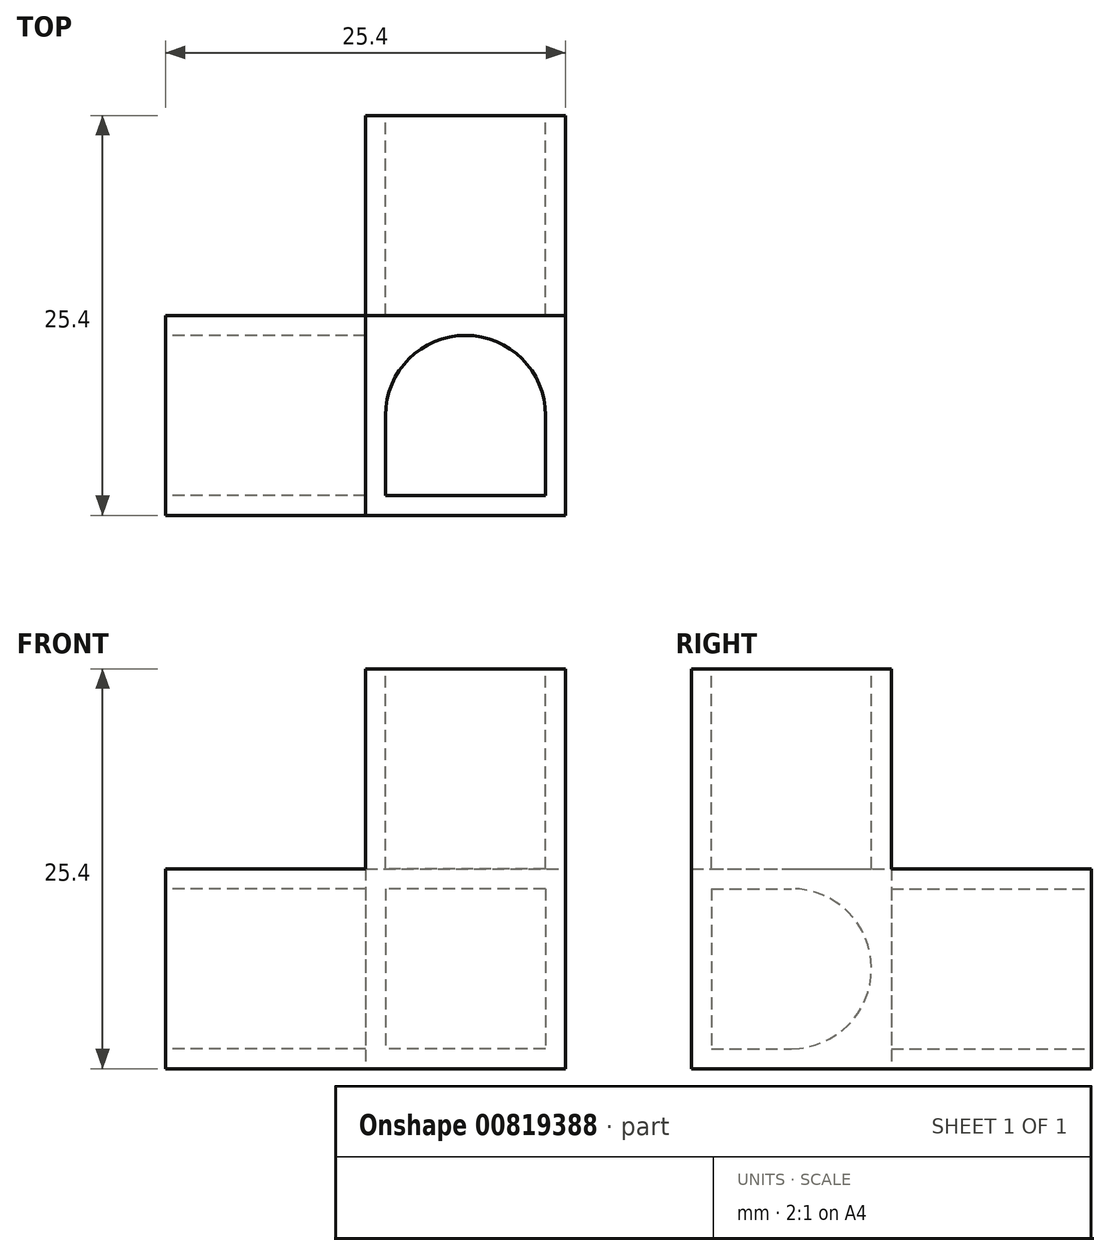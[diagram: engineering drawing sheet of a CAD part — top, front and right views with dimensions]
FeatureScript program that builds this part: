
annotation { "Feature Type Name" : "Feature", "Feature Type Description" : "" }
export const myFeature = defineFeature(function(context is Context, id is Id, definition is map)
    precondition{}
    {
        {
            var Q0;
            Q0=qCreatedBy(makeId("Top.planeOp"),FACE);
            var sketch = newSketch(context, id + "F0", { "sketchPlane" : qUnion([Q0])});
            skLineSegment(sketch, "E0", {"start": v(0, 0) * mm, "end": v(0, 12.7) * mm});
            skLineSegment(sketch, "E1", {"start": v(0, 12.7) * mm, "end": v(12.7, 12.7) * mm});
            skLineSegment(sketch, "E2", {"start": v(12.7, 12.7) * mm, "end": v(12.7, 25.4) * mm});
            skLineSegment(sketch, "E3", {"start": v(12.7, 25.4) * mm, "end": v(25.4, 25.4) * mm});
            skLineSegment(sketch, "E4", {"start": v(25.4, 25.4) * mm, "end": v(25.4, 12.7) * mm});
            skLineSegment(sketch, "E5", {"start": v(25.4, 0) * mm, "end": v(0, 0) * mm});
            skLineSegment(sketch, "E6", {"start": v(25.4, 0) * mm, "end": v(25.4, 12.7) * mm});
            skSolve(sketch);
        }
        {
            var Q0;
            Q0=qSketchRegion(id+"F0",true);
            extrude(context, id + "F1", {"entities" : qUnion([Q0]), "depth" : 12.7 * mm, "offsetDistance" : 25.4 * mm});
        }
        {
            var Q0;
            Q0=makeQuery(id+"F1.opExtrude","CAP_FACE",FACE,{"disambiguationData":[OSD([sQuery(id+"F0.wireOp",EDGE,"E0"),sQuery(id+"F0.wireOp",EDGE,"E1"),sQuery(id+"F0.wireOp",EDGE,"E2"),sQuery(id+"F0.wireOp",EDGE,"E3"),sQuery(id+"F0.wireOp",EDGE,"E4"),sQuery(id+"F0.wireOp",EDGE,"7KOMFThw-mYcV-5t9V-noh5-IcYA5axM13lC"),sQuery(id+"F0.wireOp",EDGE,"wvZKuQWc-6P0O-He2z-FqQs-M1QsOUskNR7B"),sQuery(id+"F0.wireOp",EDGE,"E5")])],"isStart":false});
            var sketch = newSketch(context, id + "F2", { "sketchPlane" : qUnion([Q0])});
            skLineSegment(sketch, "E7.bottom", {"start": v(12.7, 12.7) * mm, "end": v(25.4, 12.7) * mm});
            skLineSegment(sketch, "E7.top", {"start": v(12.7, 0) * mm, "end": v(25.4, 0) * mm});
            skLineSegment(sketch, "E7.left", {"start": v(12.7, 12.7) * mm, "end": v(12.7, 0) * mm});
            skLineSegment(sketch, "E7.right", {"start": v(25.4, 12.7) * mm, "end": v(25.4, 0) * mm});
            skSolve(sketch);
        }
        {
            var Q0;
            Q0=qSketchRegion(id+"F2",true);
            extrude(context, id + "F3", {"entities" : qUnion([Q0]), "operationType" : NewBodyOperationType.ADD, "depth" : 12.7 * mm, "offsetDistance" : 25.4 * mm});
        }
        {
            var Q0;
            Q0=makeQuery(id+"F1.opExtrude","SWEPT_FACE",FACE,{"disambiguationData":[OSD([sQuery(id+"F0.wireOp",EDGE,"E0")])]});
            var sketch = newSketch(context, id + "F4", { "sketchPlane" : qUnion([Q0])});
            skSolve(sketch);
        }
        {
            var Q0;
            Q0=makeQuery(id+"F3.opExtrude","CAP_FACE",FACE,{"disambiguationData":[OSD([sQuery(id+"F2.wireOp",EDGE,"E7.bottom"),sQuery(id+"F2.wireOp",EDGE,"E7.top"),sQuery(id+"F2.wireOp",EDGE,"E7.left"),sQuery(id+"F2.wireOp",EDGE,"E7.right")])],"isStart":false});
            var sketch = newSketch(context, id + "F5", { "sketchPlane" : qUnion([Q0])});
            skLineSegment(sketch, "E8.bottom", {"start": v(24.13, 1.27) * mm, "end": v(13.97, 1.27) * mm});
            skLineSegment(sketch, "E8.top", {"start": v(24.13, 6.35) * mm, "end": v(13.97, 6.35) * mm});
            skLineSegment(sketch, "E8.left", {"start": v(24.13, 1.27) * mm, "end": v(24.13, 6.35) * mm});
            skLineSegment(sketch, "E8.right", {"start": v(13.97, 1.27) * mm, "end": v(13.97, 6.35) * mm});
            skArc(sketch, "E9", {"start": v(24.13, 6.35) * mm, "mid": v(19.05, 11.43) * mm, "end": v(13.97, 6.35) * mm});
            skSolve(sketch);
        }
        {
            var Q0;
            Q0=qSketchRegion(id+"F5",true);
            extrude(context, id + "F6", {"entities" : qUnion([Q0]), "operationType" : NewBodyOperationType.REMOVE, "oppositeDirection" : true, "depth" : 12.7 * mm, "offsetDistance" : 25.4 * mm});
        }
        {
            var Q0;
            {var subQ0=sQuery(id+"F0.wireOp",EDGE,"E0");Q0=makeQuery(id+"F4.imprint","IMPRINT",FACE,{"disambiguationData":[TD([[makeQuery(id+"F4.imprint","IMPRINT",EDGE,{"derivedFrom":makeQuery(id+"F1.opExtrude","CAP_EDGE",EDGE,{"disambiguationData":[OSD([subQ0])],"isStart":true})}),-1.0]])]});}
            var sketch = newSketch(context, id + "F7", { "sketchPlane" : qUnion([Q0])});
            skLineSegment(sketch, "E10.bottom", {"start": v(-1.27, 11.43) * mm, "end": v(-6.35, 11.43) * mm});
            skLineSegment(sketch, "E10.top", {"start": v(-1.27, 1.27) * mm, "end": v(-6.35, 1.27) * mm});
            skLineSegment(sketch, "E10.left", {"start": v(-1.27, 11.43) * mm, "end": v(-1.27, 1.27) * mm});
            skLineSegment(sketch, "E10.right", {"start": v(-6.35, 11.43) * mm, "end": v(-6.35, 1.27) * mm});
            skArc(sketch, "E11", {"start": v(-6.35, 11.43) * mm, "mid": v(-11.43, 6.35) * mm, "end": v(-6.35, 1.27) * mm});
            skSolve(sketch);
        }
        {
            var Q0;
            Q0=qSketchRegion(id+"F7",true);
            extrude(context, id + "F8", {"entities" : qUnion([Q0]), "operationType" : NewBodyOperationType.REMOVE, "oppositeDirection" : true, "depth" : 12.7 * mm, "offsetDistance" : 25.4 * mm});
        }
        {
            var Q0;
            Q0=makeQuery(id+"F1.opExtrude","SWEPT_FACE",FACE,{"disambiguationData":[OSD([sQuery(id+"F0.wireOp",EDGE,"E3")])]});
            var sketch = newSketch(context, id + "F9", { "sketchPlane" : qUnion([Q0])});
            skLineSegment(sketch, "E12.bottom", {"start": v(-24.13, 11.43) * mm, "end": v(-13.97, 11.43) * mm});
            skLineSegment(sketch, "E12.top", {"start": v(-24.13, 1.27) * mm, "end": v(-13.97, 1.27) * mm});
            skLineSegment(sketch, "E12.left", {"start": v(-24.13, 11.43) * mm, "end": v(-24.13, 1.27) * mm});
            skLineSegment(sketch, "E12.right", {"start": v(-13.97, 11.43) * mm, "end": v(-13.97, 1.27) * mm});
            skSolve(sketch);
        }
        {
            var Q0;
            Q0=qSketchRegion(id+"F9",true);
            extrude(context, id + "F10", {"entities" : qUnion([Q0]), "operationType" : NewBodyOperationType.REMOVE, "oppositeDirection" : true, "depth" : 12.7 * mm, "offsetDistance" : 25.4 * mm});
        }
    });
